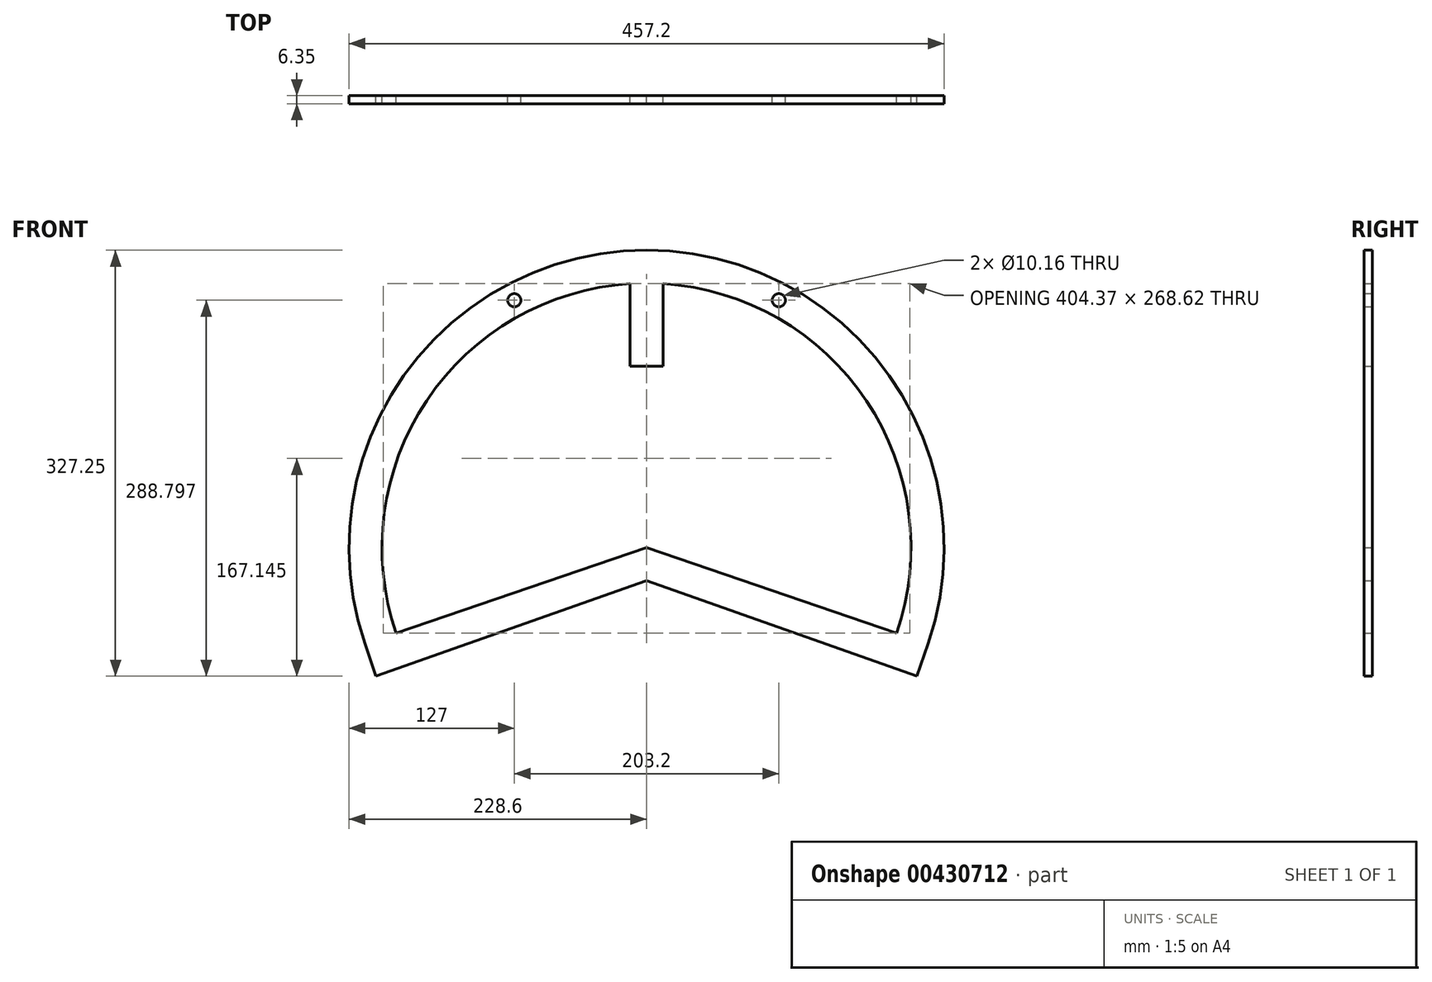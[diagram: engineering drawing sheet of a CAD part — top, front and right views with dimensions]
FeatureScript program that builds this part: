
annotation { "Feature Type Name" : "Feature", "Feature Type Description" : "" }
export const myFeature = defineFeature(function(context is Context, id is Id, definition is map)
    precondition{}
    {
        {
            var Q0;
            Q0=qCreatedBy(makeId("Front.planeOp"),FACE);
            var sketch = newSketch(context, id + "F0", { "sketchPlane" : qUnion([Q0])});
            skLineSegment(sketch, "E0", {"start": v(0, 0) * mm, "end": v(-216.28, -74.04) * mm});
            skLineSegment(sketch, "E1", {"start": v(0, 0) * mm, "end": v(216.28, -74.04) * mm});
            skArc(sketch, "E2", {"start": v(216.28, -74.04) * mm, "mid": v(0, 228.6) * mm, "end": v(-216.28, -74.04) * mm});
            skArc(sketch, "E3", {"start": v(192.25, -65.81) * mm, "mid": v(0, 203.2) * mm, "end": v(-192.25, -65.81) * mm});
            skLineSegment(sketch, "E4", {"start": v(0, -25.4) * mm, "end": v(-207.85, -98.65) * mm});
            skLineSegment(sketch, "E5", {"start": v(-207.85, -98.65) * mm, "end": v(-216.28, -74.04) * mm});
            skLineSegment(sketch, "E6", {"start": v(0, -25.4) * mm, "end": v(207.85, -98.65) * mm});
            skLineSegment(sketch, "E7", {"start": v(207.85, -98.65) * mm, "end": v(216.28, -74.04) * mm});
            skLineSegment(sketch, "E8", {"start": v(-12.7, 228.25) * mm, "end": v(-12.7, 139.35) * mm});
            skLineSegment(sketch, "E9", {"start": v(-12.7, 139.35) * mm, "end": v(12.7, 139.35) * mm});
            skLineSegment(sketch, "E10", {"start": v(12.7, 139.35) * mm, "end": v(12.7, 228.25) * mm});
            skCircle(sketch, "E11", {"center": v(-101.6, 190.15) * mm, "radius": 5.08 * mm});
            skCircle(sketch, "E12", {"center": v(101.6, 190.15) * mm, "radius": 5.08 * mm});
            skLineSegment(sketch, "E13", {"start": v(0, 27.35) * mm, "end": v(0, 217.56) * mm, "construction": true});
            skPoint(sketch, "E13.endSnap0", {"position": v(0, 203.2) * mm});
            skSolve(sketch);
        }
        {
            var Q0;
            Q0 = qSketchRegion(id + "F0", true);
            var Q1;
            {var subQ5=sQuery(id+"F0.wireOp",EDGE,"E9");Q1=makeQuery(id+"F0.imprint","IMPRINT",FACE,{"disambiguationData":[TD([[makeQuery(id+"F0.imprint","IMPRINT",EDGE,{"derivedFrom":subQ5}),1.0]])]});}
            extrude(context, id + "F1", {"entities" : qUnion([Q0, Q1]), "depth" : 6.35 * mm, "offsetDistance" : 25.4 * mm});
        }
    });
